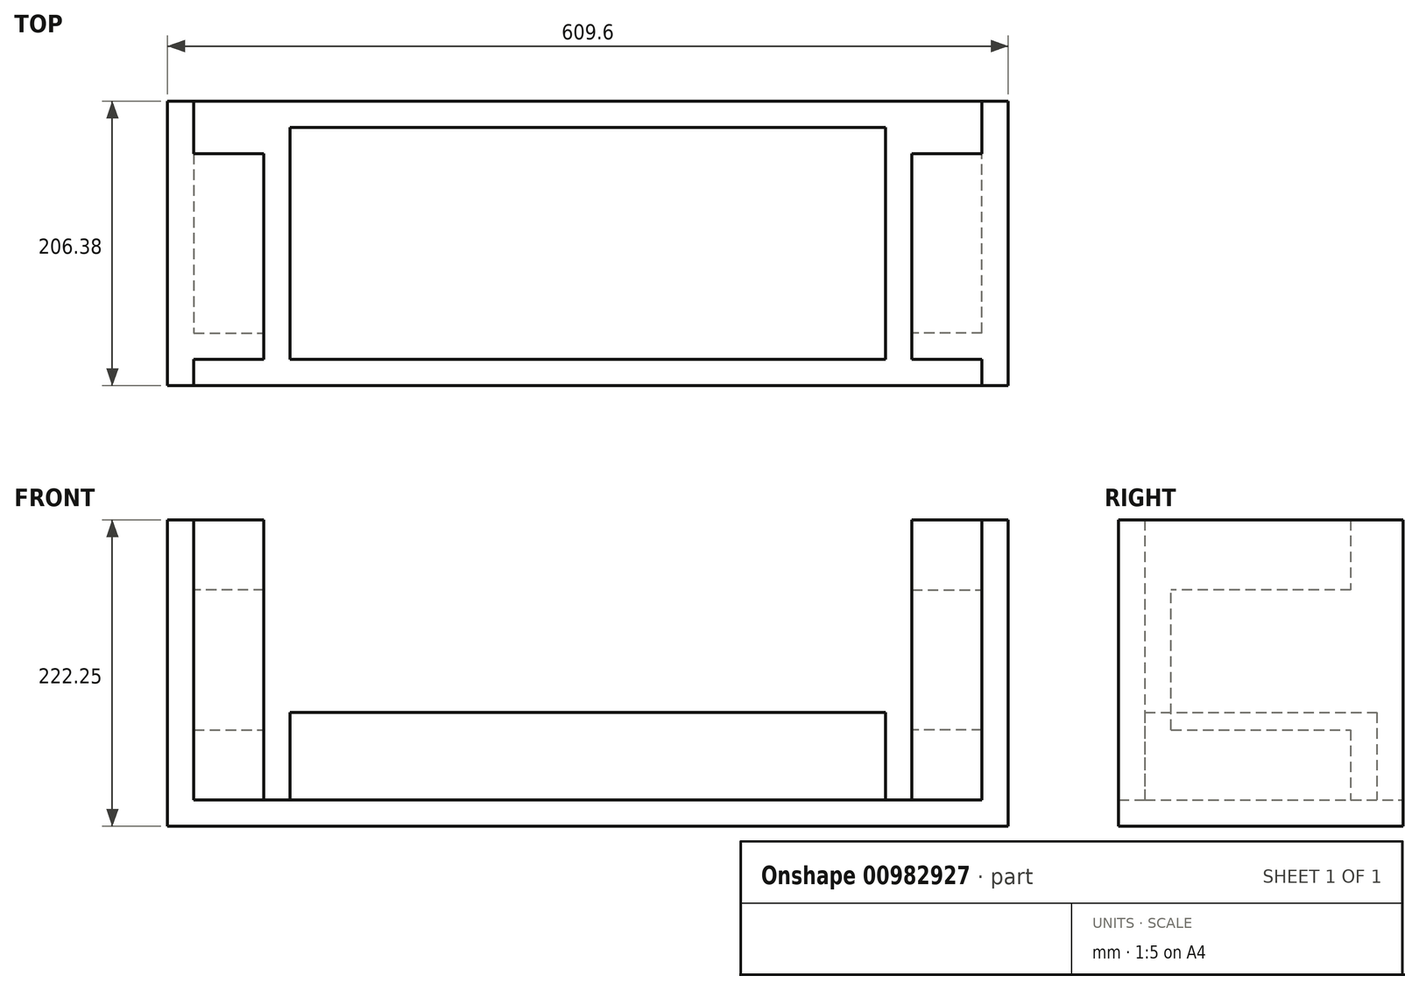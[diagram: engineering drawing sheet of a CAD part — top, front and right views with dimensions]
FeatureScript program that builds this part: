
annotation { "Feature Type Name" : "Feature", "Feature Type Description" : "" }
export const myFeature = defineFeature(function(context is Context, id is Id, definition is map)
    precondition{}
    {
        {
            var Q0;
            Q0=qCreatedBy(makeId("Top.planeOp"),FACE);
            var sketch = newSketch(context, id + "F0", { "sketchPlane" : qUnion([Q0])});
            skLineSegment(sketch, "E0.bottom", {"start": v(0, 0) * mm, "end": v(609.6, 0) * mm});
            skLineSegment(sketch, "E0.top", {"start": v(0, 206.38) * mm, "end": v(609.6, 206.38) * mm});
            skLineSegment(sketch, "E0.left", {"start": v(0, 0) * mm, "end": v(0, 206.38) * mm});
            skLineSegment(sketch, "E0.right", {"start": v(609.6, 0) * mm, "end": v(609.6, 206.38) * mm});
            skSolve(sketch);
        }
        {
            var Q0;
            Q0=makeQuery(id+"F0.imprint","IMPRINT",FACE,{"disambiguationData":[TD([[makeQuery(id+"F0.imprint","IMPRINT",EDGE,{"derivedFrom":sQuery(id+"F0.wireOp",EDGE,"E0.bottom")}),1.0]])]});
            extrude(context, id + "F1", {"entities" : qUnion([Q0]), "depth" : 19.05 * mm, "offsetDistance" : 25.4 * mm});
        }
        {
            var Q0;
            Q0=makeQuery(id+"F1.opExtrude","CAP_FACE",FACE,{"disambiguationData":[OSD([sQuery(id+"F0.wireOp",EDGE,"E0.bottom"),sQuery(id+"F0.wireOp",EDGE,"E0.top"),sQuery(id+"F0.wireOp",EDGE,"E0.left"),sQuery(id+"F0.wireOp",EDGE,"E0.right")])],"isStart":false});
            var sketch = newSketch(context, id + "F2", { "sketchPlane" : qUnion([Q0])});
            skLineSegment(sketch, "E1.bottom", {"start": v(88.9, 19.05) * mm, "end": v(520.7, 19.05) * mm});
            skLineSegment(sketch, "E1.top", {"start": v(88.9, 187.33) * mm, "end": v(520.7, 187.33) * mm});
            skLineSegment(sketch, "E1.left", {"start": v(88.9, 19.05) * mm, "end": v(88.9, 187.33) * mm});
            skLineSegment(sketch, "E1.right", {"start": v(520.7, 19.05) * mm, "end": v(520.7, 187.33) * mm});
            skSolve(sketch);
        }
        {
            var Q0;
            Q0=makeQuery(id+"F2.imprint","IMPRINT",FACE,{"disambiguationData":[TD([[makeQuery(id+"F2.imprint","IMPRINT",EDGE,{"derivedFrom":sQuery(id+"F2.wireOp",EDGE,"E1.bottom")}),1.0]])]});
            extrude(context, id + "F3", {"entities" : qUnion([Q0]), "operationType" : NewBodyOperationType.ADD, "depth" : 63.5 * mm, "offsetDistance" : 25.4 * mm});
        }
        {
            var Q0;
            Q0=makeQuery(id+"F2.imprint","IMPRINT",FACE,{"disambiguationData":[TD([[makeQuery(id+"F2.imprint","IMPRINT",EDGE,{"derivedFrom":sQuery(id+"F2.wireOp",EDGE,"E1.bottom")}),-1.0]])]});
            var sketch = newSketch(context, id + "F4", { "sketchPlane" : qUnion([Q0])});
            skLineSegment(sketch, "E2.bottom", {"start": v(0, 0) * mm, "end": v(19.05, 0) * mm});
            skLineSegment(sketch, "E2.top", {"start": v(0, 206.38) * mm, "end": v(19.05, 206.38) * mm});
            skLineSegment(sketch, "E2.left", {"start": v(0, 0) * mm, "end": v(0, 206.38) * mm});
            skLineSegment(sketch, "E2.right", {"start": v(19.05, 0) * mm, "end": v(19.05, 206.38) * mm});
            skLineSegment(sketch, "E3.bottom", {"start": v(609.6, 0) * mm, "end": v(590.55, 0) * mm});
            skLineSegment(sketch, "E3.top", {"start": v(609.6, 206.38) * mm, "end": v(590.55, 206.38) * mm});
            skLineSegment(sketch, "E3.left", {"start": v(609.6, 0) * mm, "end": v(609.6, 206.38) * mm});
            skLineSegment(sketch, "E3.right", {"start": v(590.55, 0) * mm, "end": v(590.55, 206.38) * mm});
            skSolve(sketch);
        }
        {
            var Q0;
            Q0 = qSketchRegion(id + "F4", true);
            extrude(context, id + "F5", {"entities" : qUnion([Q0]), "operationType" : NewBodyOperationType.ADD, "depth" : 203.2 * mm, "offsetDistance" : 25.4 * mm});
        }
        {
            var Q0;
            Q0=makeQuery(id+"F2.imprint","IMPRINT",FACE,{"disambiguationData":[TD([[makeQuery(id+"F2.imprint","IMPRINT",EDGE,{"derivedFrom":sQuery(id+"F2.wireOp",EDGE,"E1.bottom")}),-1.0]])]});
            var sketch = newSketch(context, id + "F6", { "sketchPlane" : qUnion([Q0])});
            skLineSegment(sketch, "E4.bottom", {"start": v(19.05, 38.1) * mm, "end": v(69.85, 38.1) * mm});
            skLineSegment(sketch, "E4.top", {"start": v(19.05, 168.28) * mm, "end": v(69.85, 168.28) * mm});
            skLineSegment(sketch, "E4.left", {"start": v(19.05, 38.1) * mm, "end": v(19.05, 168.28) * mm});
            skLineSegment(sketch, "E4.right", {"start": v(69.85, 38.1) * mm, "end": v(69.85, 168.28) * mm});
            skLineSegment(sketch, "E5.bottom", {"start": v(590.55, 38.1) * mm, "end": v(539.75, 38.1) * mm});
            skLineSegment(sketch, "E5.top", {"start": v(590.55, 168.28) * mm, "end": v(539.75, 168.28) * mm});
            skLineSegment(sketch, "E5.left", {"start": v(590.55, 38.1) * mm, "end": v(590.55, 168.28) * mm});
            skLineSegment(sketch, "E5.right", {"start": v(539.75, 38.1) * mm, "end": v(539.75, 168.28) * mm});
            skSolve(sketch);
        }
        {
            var Q0;
            Q0 = qSketchRegion(id + "F6", true);
            extrude(context, id + "F7", {"entities" : qUnion([Q0]), "operationType" : NewBodyOperationType.ADD, "depth" : 50.8 * mm, "offsetDistance" : 25.4 * mm});
        }
        {
            var Q0;
            Q0=makeQuery(id+"F5.opExtrude","SWEPT_FACE",FACE,{"disambiguationData":[OSD([sQuery(id+"F4.wireOp",EDGE,"E2.right")])]});
            var sketch = newSketch(context, id + "F8", { "sketchPlane" : qUnion([Q0])});
            skLineSegment(sketch, "E6.bottom", {"start": v(168.28, 222.25) * mm, "end": v(38.1, 222.25) * mm});
            skLineSegment(sketch, "E6.top", {"start": v(168.28, 171.45) * mm, "end": v(38.1, 171.45) * mm});
            skLineSegment(sketch, "E6.left", {"start": v(168.28, 222.25) * mm, "end": v(168.28, 171.45) * mm});
            skLineSegment(sketch, "E6.right", {"start": v(38.1, 222.25) * mm, "end": v(38.1, 171.45) * mm});
            skSolve(sketch);
        }
        {
            var Q0;
            Q0 = qSketchRegion(id + "F8", true);
            extrude(context, id + "F9", {"entities" : qUnion([Q0]), "operationType" : NewBodyOperationType.ADD, "depth" : 50.8 * mm, "offsetDistance" : 25.4 * mm});
        }
        {
            var Q0;
            Q0=makeQuery(id+"F5.opExtrude","SWEPT_FACE",FACE,{"disambiguationData":[OSD([sQuery(id+"F4.wireOp",EDGE,"E3.right")])]});
            var sketch = newSketch(context, id + "F10", { "sketchPlane" : qUnion([Q0])});
            skLineSegment(sketch, "E7.bottom", {"start": v(-168.27, 222.25) * mm, "end": v(-38.1, 222.25) * mm});
            skLineSegment(sketch, "E7.top", {"start": v(-168.27, 171.45) * mm, "end": v(-38.1, 171.45) * mm});
            skLineSegment(sketch, "E7.left", {"start": v(-168.27, 222.25) * mm, "end": v(-168.27, 171.45) * mm});
            skLineSegment(sketch, "E7.right", {"start": v(-38.1, 222.25) * mm, "end": v(-38.1, 171.45) * mm});
            skSolve(sketch);
        }
        {
            var Q0;
            Q0=makeQuery(id+"F10.imprint","IMPRINT",FACE,{"disambiguationData":[TD([[makeQuery(id+"F10.imprint","IMPRINT",EDGE,{"derivedFrom":sQuery(id+"F10.wireOp",EDGE,"E7.bottom")}),1.0]])]});
            extrude(context, id + "F11", {"entities" : qUnion([Q0]), "operationType" : NewBodyOperationType.ADD, "depth" : 50.8 * mm, "offsetDistance" : 25.4 * mm});
        }
        {
            var Q0;
            Q0=makeQuery(id+"F7.opExtrude","SWEPT_FACE",FACE,{"disambiguationData":[OSD([sQuery(id+"F6.wireOp",EDGE,"E4.bottom")])]});
            var sketch = newSketch(context, id + "F12", { "sketchPlane" : qUnion([Q0])});
            skLineSegment(sketch, "E8.bottom", {"start": v(19.05, 19.05) * mm, "end": v(69.85, 19.05) * mm});
            skLineSegment(sketch, "E8.top", {"start": v(19.05, 222.25) * mm, "end": v(69.85, 222.25) * mm});
            skLineSegment(sketch, "E8.left", {"start": v(19.05, 19.05) * mm, "end": v(19.05, 222.25) * mm});
            skLineSegment(sketch, "E8.right", {"start": v(69.85, 19.05) * mm, "end": v(69.85, 222.25) * mm});
            skLineSegment(sketch, "E9.bottom", {"start": v(539.75, 19.05) * mm, "end": v(590.55, 19.05) * mm});
            skLineSegment(sketch, "E9.top", {"start": v(539.75, 222.25) * mm, "end": v(590.55, 222.25) * mm});
            skLineSegment(sketch, "E9.left", {"start": v(539.75, 19.05) * mm, "end": v(539.75, 222.25) * mm});
            skLineSegment(sketch, "E9.right", {"start": v(590.55, 19.05) * mm, "end": v(590.55, 222.25) * mm});
            skSolve(sketch);
        }
        {
            var Q0;
            Q0 = qSketchRegion(id + "F12", true);
            extrude(context, id + "F13", {"entities" : qUnion([Q0]), "operationType" : NewBodyOperationType.ADD, "depth" : 19.05 * mm, "offsetDistance" : 25.4 * mm});
        }
    });
